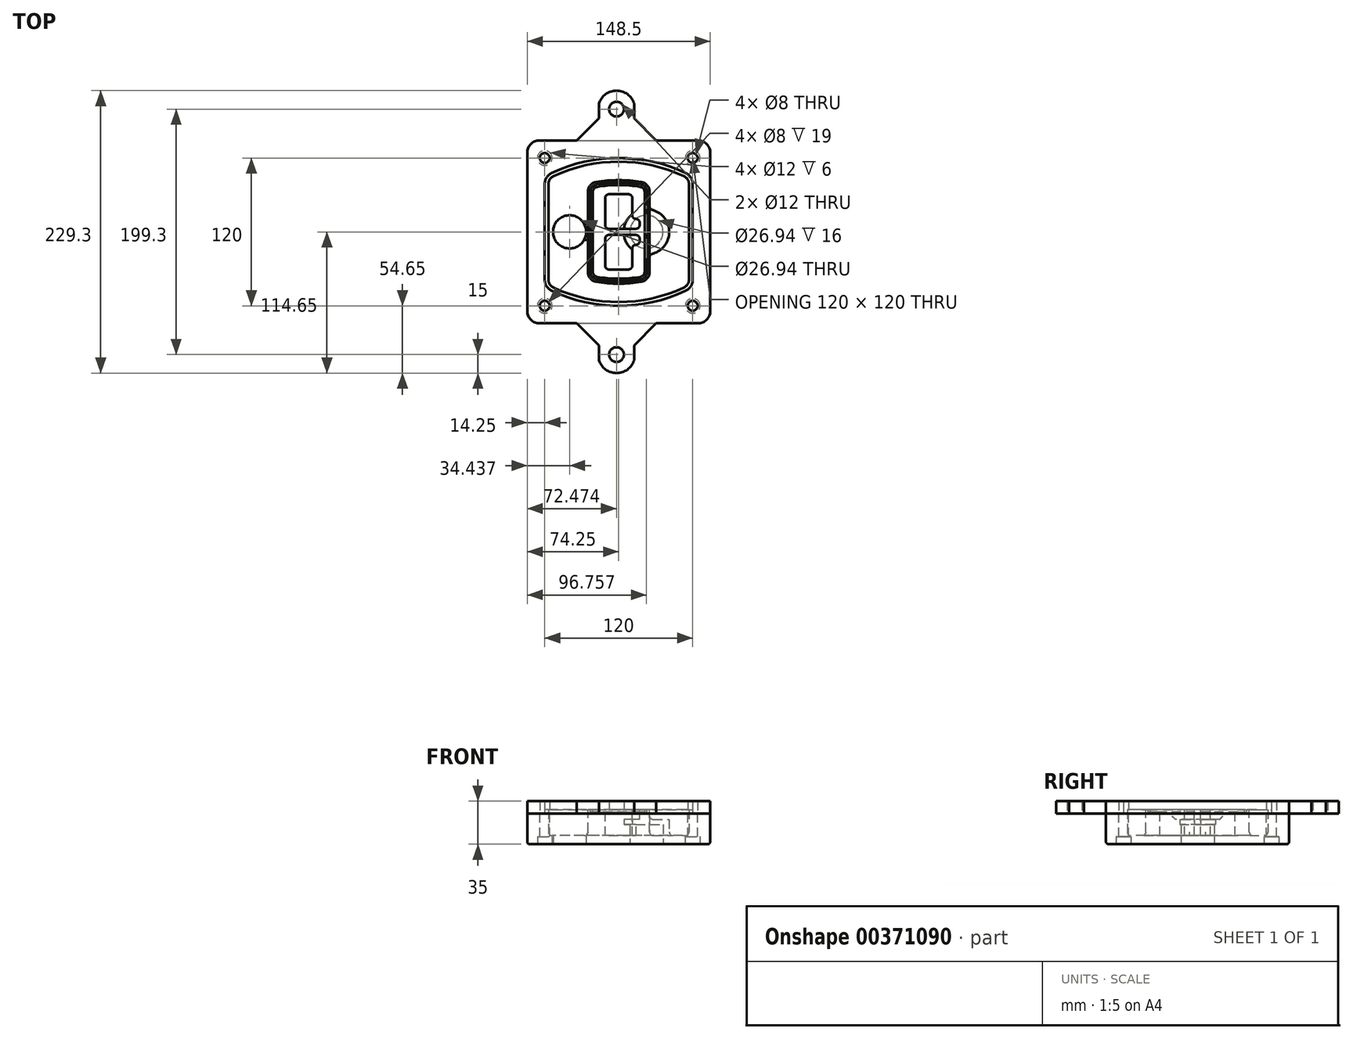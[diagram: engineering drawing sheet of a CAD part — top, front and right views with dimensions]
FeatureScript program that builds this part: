
annotation { "Feature Type Name" : "Feature", "Feature Type Description" : "" }
export const myFeature = defineFeature(function(context is Context, id is Id, definition is map)
    precondition{}
    {
        {
            var Q0;
            Q0=qCreatedBy(makeId("Top.planeOp"),FACE);
            var sketch = newSketch(context, id + "F0", { "sketchPlane" : qUnion([Q0])});
            skPoint(sketch, "E0.rect.middle", {"position": v(0, 0) * mm});
            skLineSegment(sketch, "E1.bottom", {"start": v(-64.25, -74.25) * mm, "end": v(64.25, -74.25) * mm});
            skLineSegment(sketch, "E1.top", {"start": v(-64.25, 74.25) * mm, "end": v(64.25, 74.25) * mm});
            skLineSegment(sketch, "E1.left", {"start": v(-74.25, -64.25) * mm, "end": v(-74.25, 64.25) * mm});
            skLineSegment(sketch, "E1.right", {"start": v(74.25, -64.25) * mm, "end": v(74.25, 64.25) * mm});
            skLineSegment(sketch, "E2", {"start": v(-74.25, 74.25) * mm, "end": v(74.25, -74.25) * mm, "construction": true});
            skLineSegment(sketch, "E3", {"start": v(74.25, 74.25) * mm, "end": v(-74.25, -74.25) * mm, "construction": true});
            skCircle(sketch, "E4", {"center": v(-60, 60) * mm, "radius": 4 * mm});
            skCircle(sketch, "E5", {"center": v(60, 60) * mm, "radius": 4 * mm});
            skCircle(sketch, "E6", {"center": v(60, -60) * mm, "radius": 4 * mm});
            skCircle(sketch, "E7", {"center": v(-60, -60) * mm, "radius": 4 * mm});
            skLineSegment(sketch, "E8", {"start": v(-60, 60) * mm, "end": v(60, 60) * mm, "construction": true});
            skLineSegment(sketch, "E9", {"start": v(60, 60) * mm, "end": v(60, -60) * mm, "construction": true});
            skLineSegment(sketch, "E10", {"start": v(60, -60) * mm, "end": v(-60, -60) * mm, "construction": true});
            skLineSegment(sketch, "E11", {"start": v(-60, -60) * mm, "end": v(-60, 60) * mm, "construction": true});
            skLineSegment(sketch, "E12", {"start": v(-60, 38.83) * mm, "end": v(-60, -38.83) * mm});
            skLineSegment(sketch, "E13", {"start": v(60, 38.83) * mm, "end": v(60, -38.83) * mm});
            skArc(sketch, "E14", {"start": v(54.26, 47.88) * mm, "mid": v(0, 60) * mm, "end": v(-54.26, 47.88) * mm});
            skArc(sketch, "E15", {"start": v(-54.26, -47.88) * mm, "mid": v(0, -60) * mm, "end": v(54.26, -47.88) * mm});
            skLineSegment(sketch, "E16", {"start": v(-60, 0) * mm, "end": v(60, 0) * mm, "construction": true});
            skPoint(sketch, "E17.visualSharp", {"position": v(-60, -45) * mm});
            skArc(sketch, "E17.filletArc", {"start": v(-60, -38.83) * mm, "mid": v(-58.44, -44.2) * mm, "end": v(-54.26, -47.88) * mm});
            skPoint(sketch, "E18.visualSharp", {"position": v(-60, 45) * mm});
            skArc(sketch, "E18.filletArc", {"start": v(-54.26, 47.88) * mm, "mid": v(-58.44, 44.2) * mm, "end": v(-60, 38.83) * mm});
            skPoint(sketch, "E19.visualSharp", {"position": v(60, 45) * mm});
            skArc(sketch, "E19.filletArc", {"start": v(60, 38.83) * mm, "mid": v(58.44, 44.2) * mm, "end": v(54.26, 47.88) * mm});
            skPoint(sketch, "E20.visualSharp", {"position": v(60, -45) * mm});
            skArc(sketch, "E20.filletArc", {"start": v(54.26, -47.88) * mm, "mid": v(58.44, -44.2) * mm, "end": v(60, -38.83) * mm});
            skPoint(sketch, "E21.visualSharp", {"position": v(-74.25, 74.25) * mm});
            skArc(sketch, "E21.filletArc", {"start": v(-64.25, 74.25) * mm, "mid": v(-71.32, 71.32) * mm, "end": v(-74.25, 64.25) * mm});
            skPoint(sketch, "E22.visualSharp", {"position": v(74.25, 74.25) * mm});
            skArc(sketch, "E22.filletArc", {"start": v(74.25, 64.25) * mm, "mid": v(71.32, 71.32) * mm, "end": v(64.25, 74.25) * mm});
            skPoint(sketch, "E23.visualSharp", {"position": v(74.25, -74.25) * mm});
            skArc(sketch, "E23.filletArc", {"start": v(64.25, -74.25) * mm, "mid": v(71.32, -71.32) * mm, "end": v(74.25, -64.25) * mm});
            skPoint(sketch, "E24.visualSharp", {"position": v(-74.25, -74.25) * mm});
            skArc(sketch, "E24.filletArc", {"start": v(-74.25, -64.25) * mm, "mid": v(-71.32, -71.32) * mm, "end": v(-64.25, -74.25) * mm});
            skArc(sketch, "E25.0", {"start": v(57, 38.83) * mm, "mid": v(55.9, 42.58) * mm, "end": v(52.98, 45.17) * mm});
            skLineSegment(sketch, "E25.1", {"start": v(57, 38.83) * mm, "end": v(57, -38.83) * mm});
            skArc(sketch, "E25.2", {"start": v(52.98, -45.17) * mm, "mid": v(55.9, -42.58) * mm, "end": v(57, -38.83) * mm});
            skArc(sketch, "E25.3", {"start": v(-52.98, -45.17) * mm, "mid": v(0, -57) * mm, "end": v(52.98, -45.17) * mm});
            skArc(sketch, "E25.4", {"start": v(-57, -38.83) * mm, "mid": v(-55.9, -42.58) * mm, "end": v(-52.98, -45.17) * mm});
            skArc(sketch, "E25.5", {"start": v(52.98, 45.17) * mm, "mid": v(0, 57) * mm, "end": v(-52.98, 45.17) * mm});
            skLineSegment(sketch, "E25.6", {"start": v(-57, 38.83) * mm, "end": v(-57, -38.83) * mm});
            skArc(sketch, "E25.7", {"start": v(-52.98, 45.17) * mm, "mid": v(-55.9, 42.58) * mm, "end": v(-57, 38.83) * mm});
            skArc(sketch, "E26.0", {"start": v(-55.96, 51.5) * mm, "mid": v(-61.82, 46.33) * mm, "end": v(-64, 38.83) * mm});
            skArc(sketch, "E26.1", {"start": v(55.96, 51.5) * mm, "mid": v(0, 64) * mm, "end": v(-55.96, 51.5) * mm});
            skArc(sketch, "E26.2", {"start": v(64, 38.83) * mm, "mid": v(61.82, 46.33) * mm, "end": v(55.96, 51.5) * mm});
            skLineSegment(sketch, "E26.3", {"start": v(64, 38.83) * mm, "end": v(64, -38.83) * mm});
            skArc(sketch, "E26.4", {"start": v(55.96, -51.5) * mm, "mid": v(61.82, -46.33) * mm, "end": v(64, -38.83) * mm});
            skLineSegment(sketch, "E26.5", {"start": v(-64, 38.83) * mm, "end": v(-64, -38.83) * mm});
            skArc(sketch, "E26.6", {"start": v(-55.96, -51.5) * mm, "mid": v(0, -64) * mm, "end": v(55.96, -51.5) * mm});
            skArc(sketch, "E26.7", {"start": v(-64, -38.83) * mm, "mid": v(-61.82, -46.33) * mm, "end": v(-55.96, -51.5) * mm});
            skSolve(sketch);
        }
        {
            var Q0;
            Q0=makeQuery(id+"F0.imprint","IMPRINT",FACE,{"disambiguationData":[TD([[makeQuery(id+"F0.imprint","IMPRINT",EDGE,{"derivedFrom":sQuery(id+"F0.wireOp",EDGE,"E1.bottom")}),1.0]])]});
            var Q1;
            Q1=makeQuery(id+"F0.imprint","IMPRINT",FACE,{"disambiguationData":[TD([[makeQuery(id+"F0.imprint","IMPRINT",EDGE,{"derivedFrom":sQuery(id+"F0.wireOp",EDGE,"E12")}),1.0]])]});
            var Q2;
            Q2=makeQuery(id+"F0.imprint","IMPRINT",FACE,{"disambiguationData":[TD([[makeQuery(id+"F0.imprint","IMPRINT",EDGE,{"derivedFrom":sQuery(id+"F0.wireOp",EDGE,"E25.0")}),1.0]])]});
            var Q3;
            Q3=makeQuery(id+"F0.imprint","IMPRINT",FACE,{"disambiguationData":[TD([[makeQuery(id+"F0.imprint","IMPRINT",EDGE,{"derivedFrom":sQuery(id+"F0.wireOp",EDGE,"E12")}),-1.0]])]});
            extrude(context, id + "F1", {"entities" : qUnion([Q0, Q1, Q2, Q3]), "oppositeDirection" : true, "depth" : 25 * mm});
        }
        {
            var Q0;
            Q0=makeQuery(id+"F0.imprint","IMPRINT",FACE,{"disambiguationData":[TD([[makeQuery(id+"F0.imprint","IMPRINT",EDGE,{"derivedFrom":sQuery(id+"F0.wireOp",EDGE,"E12")}),1.0]])]});
            extrude(context, id + "F2", {"entities" : qUnion([Q0]), "operationType" : NewBodyOperationType.ADD, "depth" : 3 * mm});
        }
        {
            var Q0;
            Q0=makeQuery(id+"F0.imprint","IMPRINT",FACE,{"disambiguationData":[TD([[makeQuery(id+"F0.imprint","IMPRINT",EDGE,{"derivedFrom":sQuery(id+"F0.wireOp",EDGE,"E25.0")}),1.0]])]});
            extrude(context, id + "F3", {"entities" : qUnion([Q0]), "operationType" : NewBodyOperationType.REMOVE, "oppositeDirection" : true, "depth" : 18 * mm});
        }
        {
            var Q0;
            Q0=makeQuery(id+"F2.opExtrude","CAP_FACE",FACE,{"disambiguationData":[OSD([sQuery(id+"F0.wireOp",EDGE,"E12"),sQuery(id+"F0.wireOp",EDGE,"E13"),sQuery(id+"F0.wireOp",EDGE,"E14"),sQuery(id+"F0.wireOp",EDGE,"E15"),sQuery(id+"F0.wireOp",EDGE,"E17.filletArc"),sQuery(id+"F0.wireOp",EDGE,"E18.filletArc"),sQuery(id+"F0.wireOp",EDGE,"E19.filletArc"),sQuery(id+"F0.wireOp",EDGE,"E20.filletArc"),sQuery(id+"F0.wireOp",EDGE,"E25.0"),sQuery(id+"F0.wireOp",EDGE,"E25.1"),sQuery(id+"F0.wireOp",EDGE,"E25.2"),sQuery(id+"F0.wireOp",EDGE,"E25.3"),sQuery(id+"F0.wireOp",EDGE,"E25.4"),sQuery(id+"F0.wireOp",EDGE,"E25.5"),sQuery(id+"F0.wireOp",EDGE,"E25.6"),sQuery(id+"F0.wireOp",EDGE,"E25.7")])],"isStart":false});
            var sketch = newSketch(context, id + "F4", { "sketchPlane" : qUnion([Q0])});
            skArc(sketch, "E27.0", {"start": v(-18.34, -40.45) * mm, "mid": v(0, -42) * mm, "end": v(18.34, -40.45) * mm});
            skArc(sketch, "E28.0", {"start": v(18.34, 40.45) * mm, "mid": v(0, 42) * mm, "end": v(-18.34, 40.45) * mm});
            skLineSegment(sketch, "E29", {"start": v(-25, 32.57) * mm, "end": v(-25, -32.57) * mm});
            skLineSegment(sketch, "E30", {"start": v(25, 32.57) * mm, "end": v(25, -32.57) * mm});
            skLineSegment(sketch, "E31", {"start": v(-25, 39.1) * mm, "end": v(25, 39.1) * mm, "construction": true});
            skLineSegment(sketch, "E32", {"start": v(-25, -39.1) * mm, "end": v(25, -39.1) * mm, "construction": true});
            skPoint(sketch, "E33.visualSharp", {"position": v(-25, 39.1) * mm});
            skArc(sketch, "E33.filletArc", {"start": v(-18.34, 40.45) * mm, "mid": v(-23.11, 37.73) * mm, "end": v(-25, 32.57) * mm});
            skPoint(sketch, "E34.visualSharp", {"position": v(25, 39.1) * mm});
            skArc(sketch, "E34.filletArc", {"start": v(25, 32.57) * mm, "mid": v(23.11, 37.73) * mm, "end": v(18.34, 40.45) * mm});
            skPoint(sketch, "E35.visualSharp", {"position": v(25, -39.1) * mm});
            skArc(sketch, "E35.filletArc", {"start": v(18.34, -40.45) * mm, "mid": v(23.11, -37.73) * mm, "end": v(25, -32.57) * mm});
            skPoint(sketch, "E36.visualSharp", {"position": v(-25, -39.1) * mm});
            skArc(sketch, "E36.filletArc", {"start": v(-25, -32.57) * mm, "mid": v(-23.11, -37.73) * mm, "end": v(-18.34, -40.45) * mm});
            skArc(sketch, "E37.0", {"start": v(52.98, 45.17) * mm, "mid": v(0, 57) * mm, "end": v(-52.98, 45.17) * mm});
            skArc(sketch, "E37.1", {"start": v(-52.98, 45.17) * mm, "mid": v(-55.9, 42.58) * mm, "end": v(-57, 38.83) * mm});
            skLineSegment(sketch, "E37.2", {"start": v(-57, 38.83) * mm, "end": v(-57, -38.83) * mm});
            skArc(sketch, "E37.3", {"start": v(-57, -38.83) * mm, "mid": v(-55.9, -42.58) * mm, "end": v(-52.98, -45.17) * mm});
            skArc(sketch, "E37.4", {"start": v(-52.98, -45.17) * mm, "mid": v(0, -57) * mm, "end": v(52.98, -45.17) * mm});
            skArc(sketch, "E37.5", {"start": v(52.98, -45.17) * mm, "mid": v(55.9, -42.58) * mm, "end": v(57, -38.83) * mm});
            skLineSegment(sketch, "E37.6", {"start": v(57, 38.83) * mm, "end": v(57, -38.83) * mm});
            skArc(sketch, "E37.7", {"start": v(57, 38.83) * mm, "mid": v(55.9, 42.58) * mm, "end": v(52.98, 45.17) * mm});
            skLineSegment(sketch, "E38.0", {"start": v(23, 32.57) * mm, "end": v(23, -32.57) * mm});
            skArc(sketch, "E38.1", {"start": v(18, -38.48) * mm, "mid": v(21.58, -36.44) * mm, "end": v(23, -32.57) * mm});
            skArc(sketch, "E38.2", {"start": v(-18, -38.48) * mm, "mid": v(0, -40) * mm, "end": v(18, -38.48) * mm});
            skArc(sketch, "E38.3", {"start": v(-23, -32.57) * mm, "mid": v(-21.58, -36.44) * mm, "end": v(-18, -38.48) * mm});
            skLineSegment(sketch, "E38.4", {"start": v(-23, 32.57) * mm, "end": v(-23, -32.57) * mm});
            skArc(sketch, "E38.5", {"start": v(23, 32.57) * mm, "mid": v(21.58, 36.44) * mm, "end": v(18, 38.48) * mm});
            skArc(sketch, "E38.6", {"start": v(-18, 38.48) * mm, "mid": v(-21.58, 36.44) * mm, "end": v(-23, 32.57) * mm});
            skArc(sketch, "E38.7", {"start": v(18, 38.48) * mm, "mid": v(0, 40) * mm, "end": v(-18, 38.48) * mm});
            skArc(sketch, "E39.0", {"start": v(21, 32.57) * mm, "mid": v(20.06, 35.15) * mm, "end": v(17.67, 36.5) * mm});
            skLineSegment(sketch, "E39.1", {"start": v(21, 32.57) * mm, "end": v(21, -32.57) * mm});
            skArc(sketch, "E39.2", {"start": v(17.67, -36.5) * mm, "mid": v(20.06, -35.15) * mm, "end": v(21, -32.57) * mm});
            skArc(sketch, "E39.3", {"start": v(-17.67, -36.5) * mm, "mid": v(0, -38) * mm, "end": v(17.67, -36.5) * mm});
            skArc(sketch, "E39.4", {"start": v(-21, -32.57) * mm, "mid": v(-20.06, -35.15) * mm, "end": v(-17.67, -36.5) * mm});
            skArc(sketch, "E39.5", {"start": v(17.67, 36.5) * mm, "mid": v(0, 38) * mm, "end": v(-17.67, 36.5) * mm});
            skLineSegment(sketch, "E39.6", {"start": v(-21, 32.57) * mm, "end": v(-21, -32.57) * mm});
            skArc(sketch, "E39.7", {"start": v(-17.67, 36.5) * mm, "mid": v(-20.06, 35.15) * mm, "end": v(-21, 32.57) * mm});
            skLineSegment(sketch, "E40", {"start": v(-25, 0) * mm, "end": v(25, 0) * mm, "construction": true});
            skLineSegment(sketch, "E41", {"start": v(-11, 5.5) * mm, "end": v(-11, 27.5) * mm});
            skLineSegment(sketch, "E42", {"start": v(-8, 30.5) * mm, "end": v(8, 30.5) * mm});
            skLineSegment(sketch, "E43", {"start": v(11, 27.5) * mm, "end": v(11, 13.5) * mm});
            skLineSegment(sketch, "E44", {"start": v(14, 10.5) * mm, "end": v(14, 10.5) * mm});
            skLineSegment(sketch, "E45", {"start": v(17, 7.5) * mm, "end": v(17, 5.5) * mm});
            skLineSegment(sketch, "E46", {"start": v(14, 2.5) * mm, "end": v(-8, 2.5) * mm});
            skPoint(sketch, "E47.visualSharp", {"position": v(-11, 30.5) * mm});
            skArc(sketch, "E47.filletArc", {"start": v(-8, 30.5) * mm, "mid": v(-10.12, 29.62) * mm, "end": v(-11, 27.5) * mm});
            skPoint(sketch, "E48.visualSharp", {"position": v(11, 30.5) * mm});
            skArc(sketch, "E48.filletArc", {"start": v(11, 27.5) * mm, "mid": v(10.12, 29.62) * mm, "end": v(8, 30.5) * mm});
            skPoint(sketch, "E49.visualSharp", {"position": v(11, 10.5) * mm});
            skArc(sketch, "E49.filletArc", {"start": v(11, 13.5) * mm, "mid": v(11.88, 11.38) * mm, "end": v(14, 10.5) * mm});
            skPoint(sketch, "E50.visualSharp", {"position": v(17, 10.5) * mm});
            skArc(sketch, "E50.filletArc", {"start": v(17, 7.5) * mm, "mid": v(16.12, 9.62) * mm, "end": v(14, 10.5) * mm});
            skPoint(sketch, "E51.visualSharp", {"position": v(17, 2.5) * mm});
            skArc(sketch, "E51.filletArc", {"start": v(14, 2.5) * mm, "mid": v(16.12, 3.38) * mm, "end": v(17, 5.5) * mm});
            skPoint(sketch, "E52.visualSharp", {"position": v(-11, 2.5) * mm});
            skArc(sketch, "E52.filletArc", {"start": v(-11, 5.5) * mm, "mid": v(-10.12, 3.38) * mm, "end": v(-8, 2.5) * mm});
            skLineSegment(sketch, "E53.0.MirrorCS", {"start": v(14, -2.5) * mm, "end": v(-8, -2.5) * mm});
            skArc(sketch, "E54.0.MirrorCS", {"start": v(-11, -5.5) * mm, "mid": v(-10.12, -3.38) * mm, "end": v(-8, -2.5) * mm});
            skLineSegment(sketch, "E55.0.MirrorCS", {"start": v(-11, -5.5) * mm, "end": v(-11, -27.5) * mm});
            skArc(sketch, "E56.0.MirrorCS", {"start": v(-8, -30.5) * mm, "mid": v(-10.12, -29.62) * mm, "end": v(-11, -27.5) * mm});
            skLineSegment(sketch, "E57.0.MirrorCS", {"start": v(-8, -30.5) * mm, "end": v(8, -30.5) * mm});
            skArc(sketch, "E58.0.MirrorCS", {"start": v(11, -27.5) * mm, "mid": v(10.12, -29.62) * mm, "end": v(8, -30.5) * mm});
            skLineSegment(sketch, "E59.0.MirrorCS", {"start": v(11, -27.5) * mm, "end": v(11, -13.5) * mm});
            skArc(sketch, "E60.0.MirrorCS", {"start": v(11, -13.5) * mm, "mid": v(11.88, -11.38) * mm, "end": v(14, -10.5) * mm});
            skArc(sketch, "E61.0.MirrorCS", {"start": v(17, -7.5) * mm, "mid": v(16.12, -9.62) * mm, "end": v(14, -10.5) * mm});
            skLineSegment(sketch, "E62.0.MirrorCS", {"start": v(17, -7.5) * mm, "end": v(17, -5.5) * mm});
            skArc(sketch, "E63.0.MirrorCS", {"start": v(14, -2.5) * mm, "mid": v(16.12, -3.38) * mm, "end": v(17, -5.5) * mm});
            skSolve(sketch);
        }
        {
            var Q0;
            Q0=makeQuery(id+"F4.imprint","IMPRINT",FACE,{"disambiguationData":[TD([[makeQuery(id+"F4.imprint","IMPRINT",EDGE,{"derivedFrom":sQuery(id+"F4.wireOp",EDGE,"E27.0")}),1.0]])]});
            var Q1;
            Q1=makeQuery(id+"F4.imprint","IMPRINT",FACE,{"disambiguationData":[TD([[makeQuery(id+"F4.imprint","IMPRINT",EDGE,{"derivedFrom":sQuery(id+"F4.wireOp",EDGE,"E38.0")}),-1.0]])]});
            var Q2;
            Q2=makeQuery(id+"F4.imprint","IMPRINT",FACE,{"disambiguationData":[TD([[makeQuery(id+"F4.imprint","IMPRINT",EDGE,{"derivedFrom":sQuery(id+"F4.wireOp",EDGE,"E39.0")}),1.0]])]});
            extrude(context, id + "F5", {"entities" : qUnion([Q0, Q1, Q2]), "operationType" : NewBodyOperationType.ADD, "endBound" : BoundingType.UP_TO_NEXT, "oppositeDirection" : true, "depth" : 25 * mm});
        }
        {
            var Q0;
            Q0=makeQuery(id+"F4.imprint","IMPRINT",FACE,{"disambiguationData":[TD([[makeQuery(id+"F4.imprint","IMPRINT",EDGE,{"derivedFrom":sQuery(id+"F4.wireOp",EDGE,"E38.0")}),-1.0]])]});
            extrude(context, id + "F6", {"entities" : qUnion([Q0]), "operationType" : NewBodyOperationType.REMOVE, "oppositeDirection" : true, "depth" : 2 * mm});
        }
        {
            var Q0;
            Q0=makeQuery(id+"F1.opExtrude","CAP_FACE",FACE,{"disambiguationData":[OSD([sQuery(id+"F0.wireOp",EDGE,"E1.bottom"),sQuery(id+"F0.wireOp",EDGE,"E1.top"),sQuery(id+"F0.wireOp",EDGE,"E1.left"),sQuery(id+"F0.wireOp",EDGE,"E1.right"),sQuery(id+"F0.wireOp",EDGE,"E4"),sQuery(id+"F0.wireOp",EDGE,"E5"),sQuery(id+"F0.wireOp",EDGE,"E6"),sQuery(id+"F0.wireOp",EDGE,"E7"),sQuery(id+"F0.wireOp",EDGE,"E21.filletArc"),sQuery(id+"F0.wireOp",EDGE,"E22.filletArc"),sQuery(id+"F0.wireOp",EDGE,"E23.filletArc"),sQuery(id+"F0.wireOp",EDGE,"E24.filletArc")])],"isStart":false});
            var sketch = newSketch(context, id + "F7", { "sketchPlane" : qUnion([Q0])});
            skCircle(sketch, "E64", {"center": v(22.5, 0) * mm, "radius": 13.47 * mm});
            skCircle(sketch, "E65", {"center": v(-39.81, 0) * mm, "radius": 13.47 * mm});
            skLineSegment(sketch, "E66", {"start": v(74.25, 0) * mm, "end": v(-74.25, 0) * mm});
            skCircle(sketch, "E67", {"center": v(22.5, 0) * mm, "radius": 18.47 * mm});
            skCircle(sketch, "E68", {"center": v(60, -60) * mm, "radius": 6 * mm});
            skCircle(sketch, "E69", {"center": v(-60, -60) * mm, "radius": 6 * mm});
            skCircle(sketch, "E70", {"center": v(-60, 60) * mm, "radius": 6 * mm});
            skCircle(sketch, "E71", {"center": v(60, 60) * mm, "radius": 6 * mm});
            skSolve(sketch);
        }
        {
            var Q0;
            {var subQ1=sQuery(id+"F7.wireOp",EDGE,"E66");var subQ4=sQuery(id+"F7.wireOp",EDGE,"E64");var subQ6=makeQuery(id+"F7.imprint","INTERSECT",VERTEX,{"disambiguationData":[OD(0.0)],"derivedFrom":[subQ4,subQ1]});Q0=makeQuery(id+"F7.imprint","IMPRINT",FACE,{"disambiguationData":[TD([[makeQuery(id+"F7.imprint","IMPRINT",EDGE,{"disambiguationData":[TD([[subQ6,-1.0]])],"derivedFrom":subQ4}),-1.0]])]});}
            var Q1;
            {var subQ0=sQuery(id+"F7.wireOp",EDGE,"E66");var subQ1=sQuery(id+"F7.wireOp",EDGE,"E64");var subQ3=makeQuery(id+"F7.imprint","INTERSECT",VERTEX,{"disambiguationData":[OD(0.0)],"derivedFrom":[subQ1,subQ0]});Q1=makeQuery(id+"F7.imprint","IMPRINT",FACE,{"disambiguationData":[TD([[makeQuery(id+"F7.imprint","IMPRINT",EDGE,{"disambiguationData":[TD([[subQ3,-1.0]])],"derivedFrom":subQ1}),1.0]])]});}
            var Q2;
            {var subQ0=sQuery(id+"F7.wireOp",EDGE,"E66");var subQ1=sQuery(id+"F7.wireOp",EDGE,"E64");var subQ3=makeQuery(id+"F7.imprint","INTERSECT",VERTEX,{"disambiguationData":[OD(0.0)],"derivedFrom":[subQ1,subQ0]});Q2=makeQuery(id+"F7.imprint","IMPRINT",FACE,{"disambiguationData":[TD([[makeQuery(id+"F7.imprint","IMPRINT",EDGE,{"disambiguationData":[TD([[subQ3,1.0]])],"derivedFrom":subQ1}),1.0]])]});}
            var Q3;
            {var subQ1=sQuery(id+"F7.wireOp",EDGE,"E66");var subQ4=sQuery(id+"F7.wireOp",EDGE,"E64");var subQ6=makeQuery(id+"F7.imprint","INTERSECT",VERTEX,{"disambiguationData":[OD(0.0)],"derivedFrom":[subQ4,subQ1]});Q3=makeQuery(id+"F7.imprint","IMPRINT",FACE,{"disambiguationData":[TD([[makeQuery(id+"F7.imprint","IMPRINT",EDGE,{"disambiguationData":[TD([[subQ6,1.0]])],"derivedFrom":subQ4}),-1.0]])]});}
            extrude(context, id + "F8", {"entities" : qUnion([Q0, Q1, Q2, Q3]), "operationType" : NewBodyOperationType.ADD, "oppositeDirection" : true, "depth" : 20 * mm});
        }
        {
            var Q0;
            {var subQ0=sQuery(id+"F7.wireOp",EDGE,"E66");var subQ1=sQuery(id+"F7.wireOp",EDGE,"E64");var subQ3=makeQuery(id+"F7.imprint","INTERSECT",VERTEX,{"disambiguationData":[OD(0.0)],"derivedFrom":[subQ1,subQ0]});Q0=makeQuery(id+"F7.imprint","IMPRINT",FACE,{"disambiguationData":[TD([[makeQuery(id+"F7.imprint","IMPRINT",EDGE,{"disambiguationData":[TD([[subQ3,-1.0]])],"derivedFrom":subQ1}),1.0]])]});}
            var Q1;
            {var subQ0=sQuery(id+"F7.wireOp",EDGE,"E66");var subQ1=sQuery(id+"F7.wireOp",EDGE,"E64");var subQ3=makeQuery(id+"F7.imprint","INTERSECT",VERTEX,{"disambiguationData":[OD(0.0)],"derivedFrom":[subQ1,subQ0]});Q1=makeQuery(id+"F7.imprint","IMPRINT",FACE,{"disambiguationData":[TD([[makeQuery(id+"F7.imprint","IMPRINT",EDGE,{"disambiguationData":[TD([[subQ3,1.0]])],"derivedFrom":subQ1}),1.0]])]});}
            extrude(context, id + "F9", {"entities" : qUnion([Q0, Q1]), "operationType" : NewBodyOperationType.REMOVE, "oppositeDirection" : true, "depth" : 16 * mm});
        }
        {
            var Q0;
            {var subQ0=sQuery(id+"F7.wireOp",EDGE,"E66");var subQ1=sQuery(id+"F7.wireOp",EDGE,"E65");var subQ3=makeQuery(id+"F7.imprint","INTERSECT",VERTEX,{"disambiguationData":[OD(0.0)],"derivedFrom":[subQ1,subQ0]});Q0=makeQuery(id+"F7.imprint","IMPRINT",FACE,{"disambiguationData":[TD([[makeQuery(id+"F7.imprint","IMPRINT",EDGE,{"disambiguationData":[TD([[subQ3,-1.0]])],"derivedFrom":subQ1}),1.0]])]});}
            var Q1;
            {var subQ0=sQuery(id+"F7.wireOp",EDGE,"E66");var subQ1=sQuery(id+"F7.wireOp",EDGE,"E65");var subQ3=makeQuery(id+"F7.imprint","INTERSECT",VERTEX,{"disambiguationData":[OD(0.0)],"derivedFrom":[subQ1,subQ0]});Q1=makeQuery(id+"F7.imprint","IMPRINT",FACE,{"disambiguationData":[TD([[makeQuery(id+"F7.imprint","IMPRINT",EDGE,{"disambiguationData":[TD([[subQ3,1.0]])],"derivedFrom":subQ1}),1.0]])]});}
            extrude(context, id + "F10", {"entities" : qUnion([Q0, Q1]), "operationType" : NewBodyOperationType.REMOVE, "oppositeDirection" : true, "depth" : 25 * mm});
        }
        {
            var Q0;
            Q0=makeQuery(id+"F7.imprint","IMPRINT",FACE,{"disambiguationData":[TD([[makeQuery(id+"F7.imprint","IMPRINT",EDGE,{"derivedFrom":sQuery(id+"F7.wireOp",EDGE,"E68")}),1.0]])]});
            var Q1;
            Q1=makeQuery(id+"F7.imprint","IMPRINT",FACE,{"disambiguationData":[TD([[makeQuery(id+"F7.imprint","IMPRINT",EDGE,{"derivedFrom":makeQuery(id+"F1.opExtrude","CAP_EDGE",EDGE,{"disambiguationData":[OSD([sQuery(id+"F0.wireOp",EDGE,"E5")])],"isStart":false})}),-1.0]])]});
            var Q2;
            Q2=makeQuery(id+"F7.imprint","IMPRINT",FACE,{"disambiguationData":[TD([[makeQuery(id+"F7.imprint","IMPRINT",EDGE,{"derivedFrom":sQuery(id+"F7.wireOp",EDGE,"E69")}),1.0]])]});
            var Q3;
            Q3=makeQuery(id+"F7.imprint","IMPRINT",FACE,{"disambiguationData":[TD([[makeQuery(id+"F7.imprint","IMPRINT",EDGE,{"derivedFrom":makeQuery(id+"F1.opExtrude","CAP_EDGE",EDGE,{"disambiguationData":[OSD([sQuery(id+"F0.wireOp",EDGE,"E4")])],"isStart":false})}),-1.0]])]});
            var Q4;
            Q4=makeQuery(id+"F7.imprint","IMPRINT",FACE,{"disambiguationData":[TD([[makeQuery(id+"F7.imprint","IMPRINT",EDGE,{"derivedFrom":sQuery(id+"F7.wireOp",EDGE,"E70")}),1.0]])]});
            var Q5;
            Q5=makeQuery(id+"F7.imprint","IMPRINT",FACE,{"disambiguationData":[TD([[makeQuery(id+"F7.imprint","IMPRINT",EDGE,{"derivedFrom":makeQuery(id+"F1.opExtrude","CAP_EDGE",EDGE,{"disambiguationData":[OSD([sQuery(id+"F0.wireOp",EDGE,"E7")])],"isStart":false})}),-1.0]])]});
            var Q6;
            Q6=makeQuery(id+"F7.imprint","IMPRINT",FACE,{"disambiguationData":[TD([[makeQuery(id+"F7.imprint","IMPRINT",EDGE,{"derivedFrom":sQuery(id+"F7.wireOp",EDGE,"E71")}),1.0]])]});
            var Q7;
            Q7=makeQuery(id+"F7.imprint","IMPRINT",FACE,{"disambiguationData":[TD([[makeQuery(id+"F7.imprint","IMPRINT",EDGE,{"derivedFrom":makeQuery(id+"F1.opExtrude","CAP_EDGE",EDGE,{"disambiguationData":[OSD([sQuery(id+"F0.wireOp",EDGE,"E6")])],"isStart":false})}),-1.0]])]});
            extrude(context, id + "F11", {"entities" : qUnion([Q0, Q1, Q2, Q3, Q4, Q5, Q6, Q7]), "operationType" : NewBodyOperationType.REMOVE, "oppositeDirection" : true, "depth" : 6 * mm});
        }
        {
            var Q0;
            Q0=makeQuery(id+"F9.boolean.opBoolean","COPY",FACE,{"derivedFrom":makeQuery(id+"F9.opExtrude","CAP_FACE",FACE,{"disambiguationData":[OSD([sQuery(id+"F7.wireOp",EDGE,"E64")])],"isStart":false})});
            var sketch = newSketch(context, id + "F12", { "sketchPlane" : qUnion([Q0])});
            skArc(sketch, "E72.0", {"start": v(11, 14.45) * mm, "mid": v(6.45, 9.13) * mm, "end": v(4.2, 2.5) * mm});
            skArc(sketch, "E72.1", {"start": v(4.2, -2.5) * mm, "mid": v(6.45, -9.13) * mm, "end": v(11, -14.45) * mm});
            skLineSegment(sketch, "E73", {"start": v(4.2, -2.5) * mm, "end": v(14, -2.5) * mm});
            skLineSegment(sketch, "E74.0", {"start": v(14, 2.5) * mm, "end": v(4.2, 2.5) * mm});
            skArc(sketch, "E74.1", {"start": v(14, 2.5) * mm, "mid": v(16.12, 3.38) * mm, "end": v(17, 5.5) * mm});
            skLineSegment(sketch, "E74.2", {"start": v(17, 7.5) * mm, "end": v(17, 5.5) * mm});
            skArc(sketch, "E74.3", {"start": v(17, 7.5) * mm, "mid": v(16.12, 9.62) * mm, "end": v(14, 10.5) * mm});
            skArc(sketch, "E74.4", {"start": v(11, 13.5) * mm, "mid": v(11.88, 11.38) * mm, "end": v(14, 10.5) * mm});
            skLineSegment(sketch, "E74.5", {"start": v(11, 14.45) * mm, "end": v(11, 13.5) * mm});
            skLineSegment(sketch, "E74.7", {"start": v(14, -2.5) * mm, "end": v(4.2, -2.5) * mm});
            skArc(sketch, "E74.8", {"start": v(14, -2.5) * mm, "mid": v(16.12, -3.38) * mm, "end": v(17, -5.5) * mm});
            skLineSegment(sketch, "E74.9", {"start": v(17, -7.5) * mm, "end": v(17, -5.5) * mm});
            skArc(sketch, "E74.10", {"start": v(17, -7.5) * mm, "mid": v(16.12, -9.62) * mm, "end": v(14, -10.5) * mm});
            skArc(sketch, "E74.11", {"start": v(11, -13.5) * mm, "mid": v(11.88, -11.38) * mm, "end": v(14, -10.5) * mm});
            skLineSegment(sketch, "E74.12", {"start": v(11, -14.45) * mm, "end": v(11, -13.5) * mm});
            skPoint(sketch, "E75.orphan", {"position": v(11, -27.5) * mm});
            skPoint(sketch, "E76.orphan", {"position": v(-8, -2.5) * mm});
            skPoint(sketch, "E77.orphan", {"position": v(-8, 2.5) * mm});
            skPoint(sketch, "E78.orphan", {"position": v(11, 27.5) * mm});
            skSolve(sketch);
        }
        {
            var Q0;
            {var subQ7=sQuery(id+"F12.wireOp",EDGE,"E72.0");var subQ14=sQuery(id+"F12.wireOp",EDGE,"E72.1");var subQ16=sQuery(id+"F12.wireOp",EDGE,"E74.1");var subQ18=sQuery(id+"F12.wireOp",EDGE,"E74.8");Q0=qUnion([makeQuery(id+"F12.imprint","IMPRINT",FACE,{"disambiguationData":[TD([[makeQuery(id+"F12.imprint","IMPRINT",EDGE,{"derivedFrom":subQ7}),1.0]])]}),makeQuery(id+"F12.imprint","IMPRINT",FACE,{"disambiguationData":[TD([[makeQuery(id+"F12.imprint","IMPRINT",EDGE,{"derivedFrom":subQ14}),1.0]])]}),makeQuery(id+"F12.imprint","IMPRINT",FACE,{"disambiguationData":[TD([[makeQuery(id+"F12.imprint","IMPRINT",EDGE,{"derivedFrom":subQ16}),1.0]])]}),makeQuery(id+"F12.imprint","IMPRINT",FACE,{"disambiguationData":[TD([[makeQuery(id+"F12.imprint","IMPRINT",EDGE,{"derivedFrom":subQ18}),-1.0]])]})]);}
            var Q1;
            Q1=makeQuery(id+"F5.boolean.opBoolean","SPLIT",FACE,{"disambiguationData":[TD([makeQuery(id+"F5.opExtrude","SWEPT_FACE",FACE,{"disambiguationData":[OSD([sQuery(id+"F4.wireOp",EDGE,"E41")])]})])],"derivedFrom":makeQuery(id+"F3.boolean.opBoolean","COPY",FACE,{"derivedFrom":makeQuery(id+"F3.opExtrude","CAP_FACE",FACE,{"disambiguationData":[OSD([sQuery(id+"F0.wireOp",EDGE,"E25.0"),sQuery(id+"F0.wireOp",EDGE,"E25.1"),sQuery(id+"F0.wireOp",EDGE,"E25.2"),sQuery(id+"F0.wireOp",EDGE,"E25.3"),sQuery(id+"F0.wireOp",EDGE,"E25.4"),sQuery(id+"F0.wireOp",EDGE,"E25.5"),sQuery(id+"F0.wireOp",EDGE,"E25.6"),sQuery(id+"F0.wireOp",EDGE,"E25.7")])],"isStart":false})})});
            extrude(context, id + "F13", {"entities" : qUnion([Q0]), "operationType" : NewBodyOperationType.REMOVE, "endBound" : BoundingType.UP_TO_SURFACE, "endBoundEntityFace" : qUnion([Q1]), "depth" : 25 * mm});
        }
        {
            var Q0;
            Q0=makeQuery(id+"F3.boolean.opBoolean","COPY",EDGE,{"derivedFrom":makeQuery(id+"F3.opExtrude","CAP_EDGE",EDGE,{"disambiguationData":[OSD([sQuery(id+"F0.wireOp",EDGE,"E25.6")])],"isStart":false})});
            var Q1;
            Q1=makeQuery(id+"F8.boolean.opBoolean","INTERSECT",EDGE,{"derivedFrom":[makeQuery(id+"F5.opExtrude","SWEPT_FACE",FACE,{"disambiguationData":[OSD([sQuery(id+"F4.wireOp",EDGE,"E30")])]}),makeQuery(id+"F8.opExtrude","CAP_FACE",FACE,{"disambiguationData":[OSD([sQuery(id+"F7.wireOp",EDGE,"E67")])],"isStart":false})]});
            var Q2;
            Q2=makeQuery(id+"F8.boolean.opBoolean","INTERSECT",EDGE,{"disambiguationData":[OD(1.0)],"derivedFrom":[makeQuery(id+"F5.opExtrude","SWEPT_FACE",FACE,{"disambiguationData":[OSD([sQuery(id+"F4.wireOp",EDGE,"E30")])]}),makeQuery(id+"F8.opExtrude","SWEPT_FACE",FACE,{"disambiguationData":[OSD([sQuery(id+"F7.wireOp",EDGE,"E67")])]})]});
            var Q3;
            {var subQ0=sQuery(id+"F4.wireOp",EDGE,"E30");Q3=makeQuery(id+"F8.boolean.opBoolean","SPLIT",EDGE,{"disambiguationData":[TD([makeQuery(id+"F5.opExtrude","SWEPT_FACE",FACE,{"disambiguationData":[OSD([sQuery(id+"F4.wireOp",EDGE,"E35.filletArc")])]})])],"derivedFrom":makeQuery(id+"F5.opExtrude","CAP_EDGE",EDGE,{"disambiguationData":[OSD([subQ0])],"isStart":false})});}
            var Q4;
            {var subQ0=sQuery(id+"F0.wireOp",EDGE,"E25.7");var subQ1=sQuery(id+"F0.wireOp",EDGE,"E25.1");var subQ2=sQuery(id+"F0.wireOp",EDGE,"E25.6");var subQ3=sQuery(id+"F0.wireOp",EDGE,"E25.5");var subQ4=sQuery(id+"F0.wireOp",EDGE,"E25.4");var subQ5=sQuery(id+"F0.wireOp",EDGE,"E25.0");var subQ6=sQuery(id+"F0.wireOp",EDGE,"E25.2");var subQ7=sQuery(id+"F0.wireOp",EDGE,"E25.3");Q4=makeQuery(id+"F8.boolean.opBoolean","INTERSECT",EDGE,{"derivedFrom":[makeQuery(id+"F5.boolean.opBoolean","SPLIT",FACE,{"disambiguationData":[TD([makeQuery(id+"F2.opExtrude","SWEPT_FACE",FACE,{"disambiguationData":[OSD([subQ5])]})])],"derivedFrom":makeQuery(id+"F3.boolean.opBoolean","COPY",FACE,{"derivedFrom":makeQuery(id+"F3.opExtrude","CAP_FACE",FACE,{"disambiguationData":[OSD([subQ5,subQ1,subQ6,subQ7,subQ4,subQ3,subQ2,subQ0])],"isStart":false})})}),makeQuery(id+"F8.opExtrude","SWEPT_FACE",FACE,{"disambiguationData":[OSD([sQuery(id+"F7.wireOp",EDGE,"E67")])]})]});}
            var Q5;
            Q5=makeQuery(id+"F8.boolean.opBoolean","INTERSECT",EDGE,{"disambiguationData":[OD(0.0)],"derivedFrom":[makeQuery(id+"F5.opExtrude","SWEPT_FACE",FACE,{"disambiguationData":[OSD([sQuery(id+"F4.wireOp",EDGE,"E30")])]}),makeQuery(id+"F8.opExtrude","SWEPT_FACE",FACE,{"disambiguationData":[OSD([sQuery(id+"F7.wireOp",EDGE,"E67")])]})]});
            fillet(context, id + "F14", {"entities" : qUnion([Q0, Q1, Q2, Q3, Q4, Q5]), "radius" : 3 * mm, "tangentPropagation" : true, "allowEdgeOverflow" : false});
        }
        {
            var Q0;
            Q0=makeQuery(id+"F1.opExtrude","CAP_EDGE",EDGE,{"disambiguationData":[OSD([sQuery(id+"F0.wireOp",EDGE,"E1.bottom")])],"isStart":false});
            fillet(context, id + "F15", {"entities" : qUnion([Q0]), "radius" : 2 * mm, "tangentPropagation" : true, "allowEdgeOverflow" : false});
        }
        {
            var Q0;
            {var subQ0=sQuery(id+"F0.wireOp",EDGE,"E21.filletArc");var subQ1=sQuery(id+"F0.wireOp",EDGE,"E7");var subQ2=sQuery(id+"F0.wireOp",EDGE,"E6");var subQ3=sQuery(id+"F0.wireOp",EDGE,"E5");var subQ4=sQuery(id+"F0.wireOp",EDGE,"E4");var subQ5=sQuery(id+"F0.wireOp",EDGE,"E22.filletArc");var subQ6=sQuery(id+"F0.wireOp",EDGE,"E1.bottom");var subQ7=sQuery(id+"F0.wireOp",EDGE,"E1.right");var subQ8=sQuery(id+"F0.wireOp",EDGE,"E1.top");var subQ9=sQuery(id+"F0.wireOp",EDGE,"E1.left");var subQ10=sQuery(id+"F0.wireOp",EDGE,"E23.filletArc");var subQ11=sQuery(id+"F0.wireOp",EDGE,"E24.filletArc");Q0=makeQuery(id+"F2.boolean.opBoolean","SPLIT",FACE,{"disambiguationData":[TD([makeQuery(id+"F1.opExtrude","SWEPT_FACE",FACE,{"disambiguationData":[OSD([subQ6])]})])],"derivedFrom":makeQuery(id+"F1.opExtrude","CAP_FACE",FACE,{"disambiguationData":[OSD([subQ6,subQ8,subQ9,subQ7,subQ4,subQ3,subQ2,subQ1,subQ0,subQ5,subQ10,subQ11])],"isStart":true})});}
            var sketch = newSketch(context, id + "F16", { "sketchPlane" : qUnion([Q0])});
            skArc(sketch, "E79", {"start": v(12.5, 104.25) * mm, "mid": v(-1.78, 114.65) * mm, "end": v(-16.05, 104.25) * mm});
            skCircle(sketch, "E80", {"center": v(-1.78, 99.65) * mm, "radius": 6 * mm});
            skLineSegment(sketch, "E81", {"start": v(-16.05, 104.25) * mm, "end": v(-16.05, 92.25) * mm});
            skLineSegment(sketch, "E82", {"start": v(12.5, 104.25) * mm, "end": v(12.5, 92.25) * mm});
            skLineSegment(sketch, "E83", {"start": v(-16.05, 92.25) * mm, "end": v(-34.05, 74.25) * mm});
            skLineSegment(sketch, "E84", {"start": v(12.5, 92.25) * mm, "end": v(30.5, 74.25) * mm});
            skLineSegment(sketch, "E85", {"start": v(-60, 0) * mm, "end": v(60, 0) * mm});
            skLineSegment(sketch, "E86.MirrorCS", {"start": v(-16.05, -92.25) * mm, "end": v(-34.05, -74.25) * mm});
            skLineSegment(sketch, "E87.MirrorCS", {"start": v(12.5, -104.25) * mm, "end": v(12.5, -92.25) * mm});
            skLineSegment(sketch, "E88.MirrorCS", {"start": v(-16.05, -104.25) * mm, "end": v(-16.05, -92.25) * mm});
            skLineSegment(sketch, "E89.MirrorCS", {"start": v(12.5, -92.25) * mm, "end": v(30.5, -74.25) * mm});
            skCircle(sketch, "E90.MirrorC", {"center": v(-1.78, -99.65) * mm, "radius": 6 * mm});
            skArc(sketch, "E91.MirrorCS", {"start": v(12.5, -104.25) * mm, "mid": v(-1.78, -114.65) * mm, "end": v(-16.05, -104.25) * mm});
            skLineSegment(sketch, "E92", {"start": v(-1.78, 99.65) * mm, "end": v(-1.78, 74.25) * mm, "construction": true});
            skPoint(sketch, "E92.endSnap0", {"position": v(0, 74.25) * mm});
            skSolve(sketch);
        }
        {
            var Q0;
            Q0=makeQuery(id+"F16.imprint","IMPRINT",FACE,{"disambiguationData":[TD([[makeQuery(id+"F16.imprint","IMPRINT",EDGE,{"derivedFrom":sQuery(id+"F16.wireOp",EDGE,"E79")}),1.0]])]});
            var Q1;
            {var subQ1=sQuery(id+"F16.wireOp",EDGE,"E86.MirrorCS");Q1=makeQuery(id+"F16.imprint","IMPRINT",FACE,{"disambiguationData":[TD([[makeQuery(id+"F16.imprint","IMPRINT",EDGE,{"derivedFrom":subQ1}),-1.0]])]});}
            var Q2;
            Q2=makeQuery(id+"F16.imprint","IMPRINT",FACE,{"disambiguationData":[TD([[makeQuery(id+"F16.imprint","IMPRINT",EDGE,{"derivedFrom":makeQuery(id+"F1.opExtrude","CAP_EDGE",EDGE,{"disambiguationData":[OSD([sQuery(id+"F0.wireOp",EDGE,"E1.left")])],"isStart":true})}),-1.0]])]});
            extrude(context, id + "F17", {"entities" : qUnion([Q0, Q1, Q2]), "depth" : 10 * mm});
        }
    });
